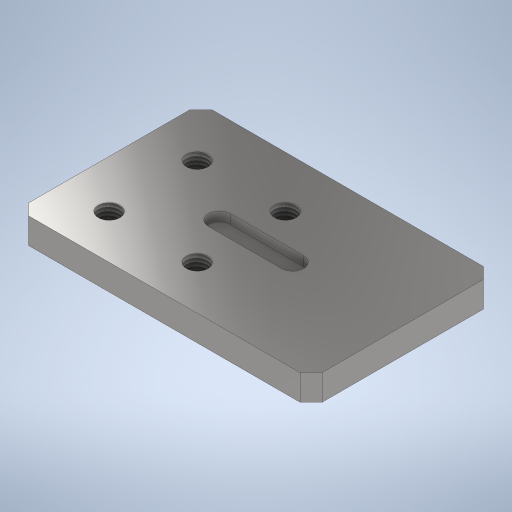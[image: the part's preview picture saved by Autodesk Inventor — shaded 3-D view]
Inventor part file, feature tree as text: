
AUTODESK INVENTOR PART (.ipt)
format: ipt  version: 2024 (Build 280153000, 153)  size: 288,768 bytes
history: native  units: mm
features: other x4, sketch x3, extrude x2, chamfer x1, hole x1, pattern_linear x1
ambient origin geometry x8: Origin, YZ Plane, XZ Plane, XY Plane, X Axis, Y Axis, Z Axis, Center Point
bodies: Volumenkörper1 (feature_tree)
feature tree (12):
  other  "Tabelle"
  other  "variante-01"
  other  "variante-02"
  other  "variante-03"
  extrude  "Extrusion1"  Depth=2.0mm TaperAngle=45.0deg
  chamfer  "Fasen1"  [1 undecoded]
  hole  "Bohrung1"  [1 undecoded]
  extrude  "Extrusion2"  Depth=24.0mm
  pattern_linear  "Rechteckige Anordnung2"  Count1=2  [1 undecoded]
  sketch  "Skizze1"  dims[d3=0.0mm d5=2.0mm d6=45.0deg]
  sketch  "Skizze2"  dims[d9=5.917468mm]
  sketch  "Skizze3"  dims[d11=4.0mm d12=2.0mm d13=90.0deg d14=8.0mm d15=20.594885mm d19=0.0mm d25=20.0mm d27=24.0mm d28=20.0mm d30=24.0mm]
note: 3 required parameter values undecoded (feature->parameter linkage not recoverable at this tier; creation-order binding heuristic only, values carry confidence <= 0.55)
